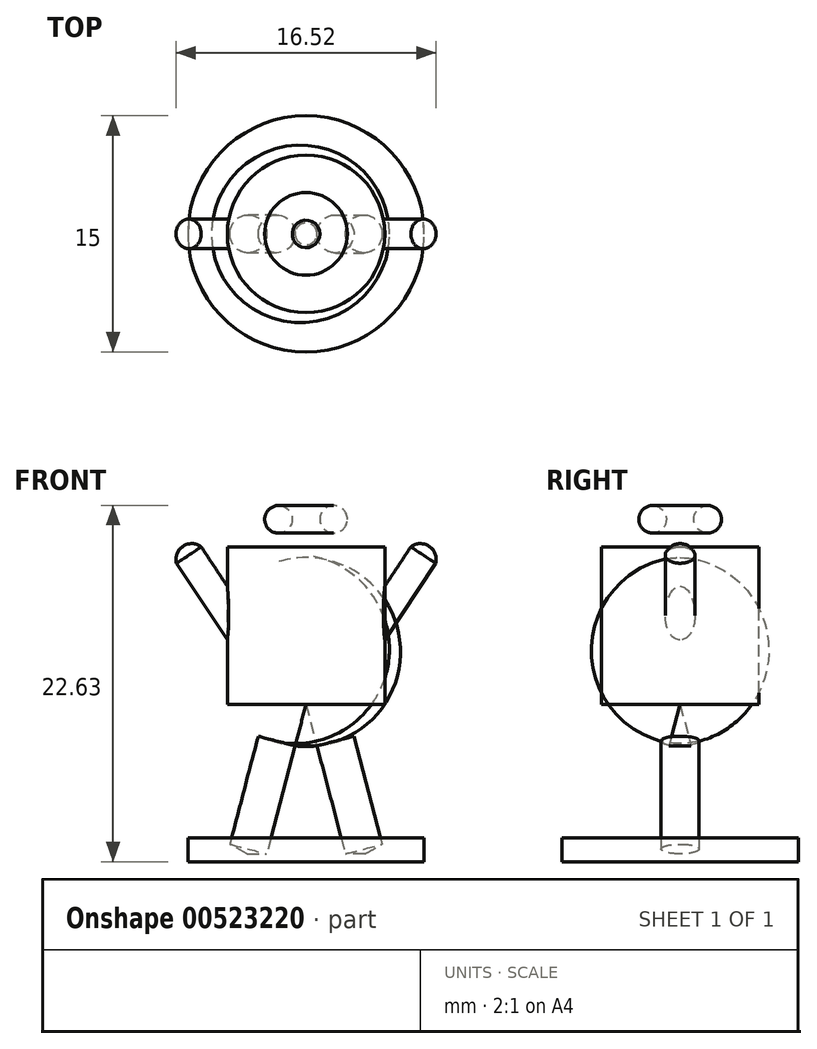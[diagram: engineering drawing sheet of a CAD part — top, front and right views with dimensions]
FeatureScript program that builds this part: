
annotation { "Feature Type Name" : "Feature", "Feature Type Description" : "" }
export const myFeature = defineFeature(function(context is Context, id is Id, definition is map)
    precondition{}
    {
        {
            var Q0;
            Q0=qCreatedBy(makeId("Front.planeOp"),FACE);
            var sketch = newSketch(context, id + "F0", { "sketchPlane" : qUnion([Q0])});
            skLineSegment(sketch, "E0.bottom", {"start": v(-5, 2.5) * mm, "end": v(5, 2.5) * mm});
            skLineSegment(sketch, "E0.top", {"start": v(-5, -7.5) * mm, "end": v(5, -7.5) * mm});
            skLineSegment(sketch, "E0.left", {"start": v(-5, 2.5) * mm, "end": v(-5, -7.5) * mm});
            skLineSegment(sketch, "E0.right", {"start": v(5, 2.5) * mm, "end": v(5, -7.5) * mm});
            skArc(sketch, "E1", {"start": v(5, 2.5) * mm, "mid": v(0, 7.5) * mm, "end": v(-5, 2.5) * mm});
            skCircle(sketch, "E2", {"center": v(-1.75, 4.25) * mm, "radius": 0.88 * mm});
            skCircle(sketch, "E3.MirrorC", {"center": v(1.75, 4.25) * mm, "radius": 0.88 * mm});
            skLineSegment(sketch, "E4.MirrorCS", {"start": v(-5, 0) * mm, "end": v(-5, -3.42) * mm});
            skLineSegment(sketch, "E5.bottom", {"start": v(5, -7.5) * mm, "end": v(2.5, -7.5) * mm});
            skLineSegment(sketch, "E6", {"start": v(0, 7.5) * mm, "end": v(0, 0) * mm});
            skLineSegment(sketch, "E7", {"start": v(0, 2.5) * mm, "end": v(0, -7.5) * mm});
            skLineSegment(sketch, "E8.MirrorCS", {"start": v(-0.02, -5) * mm, "end": v(0, 5) * mm});
            skLineSegment(sketch, "E9", {"start": v(5, 0) * mm, "end": v(6.66, 2.5) * mm});
            skLineSegment(sketch, "E10", {"start": v(6.66, 2.5) * mm, "end": v(8.23, 1.46) * mm});
            skLineSegment(sketch, "E11", {"start": v(8.23, 1.46) * mm, "end": v(5, -3.42) * mm});
            skArc(sketch, "E12", {"start": v(8.23, 1.46) * mm, "mid": v(7.82, 2.54) * mm, "end": v(6.66, 2.5) * mm});
            skLineSegment(sketch, "E13.MirrorCS", {"start": v(-6.68, 2.52) * mm, "end": v(-8.25, 1.48) * mm});
            skArc(sketch, "E14.MirrorCS", {"start": v(-8.25, 1.48) * mm, "mid": v(-7.84, 2.56) * mm, "end": v(-6.68, 2.52) * mm});
            skLineSegment(sketch, "E15.MirrorCS", {"start": v(-5.03, 0.01) * mm, "end": v(-5.03, -3.4) * mm});
            skLineSegment(sketch, "E16.MirrorCS", {"start": v(-8.25, 1.48) * mm, "end": v(-5.03, -3.4) * mm});
            skLineSegment(sketch, "E17.MirrorCS", {"start": v(-5.03, 0.01) * mm, "end": v(-6.68, 2.52) * mm});
            skLineSegment(sketch, "E18", {"start": v(0, -7.5) * mm, "end": v(0, -9.4) * mm});
            skLineSegment(sketch, "E19", {"start": v(2.5, -17) * mm, "end": v(3.75, -17) * mm});
            skLineSegment(sketch, "E20", {"start": v(-3.75, -17) * mm, "end": v(-2.5, -17) * mm});
            skLineSegment(sketch, "E21", {"start": v(7.45, 1.98) * mm, "end": v(5, -1.7) * mm});
            skLineSegment(sketch, "E22", {"start": v(5, -1.7) * mm, "end": v(7.45, 1.98) * mm});
            skLineSegment(sketch, "E23", {"start": v(7.82, 2.54) * mm, "end": v(7.45, 1.98) * mm});
            skLineSegment(sketch, "E24", {"start": v(0, -7.5) * mm, "end": v(2.5, -17) * mm});
            skLineSegment(sketch, "E25", {"start": v(3.75, -17) * mm, "end": v(1.25, -7.5) * mm});
            skLineSegment(sketch, "E26", {"start": v(1.25, -7.5) * mm, "end": v(0, -7.5) * mm});
            skLineSegment(sketch, "E27", {"start": v(0, -7.5) * mm, "end": v(-2.5, -17) * mm});
            skLineSegment(sketch, "E28", {"start": v(-3.75, -17) * mm, "end": v(-1.25, -7.5) * mm});
            skLineSegment(sketch, "E29", {"start": v(-1.25, -7.5) * mm, "end": v(0, -7.5) * mm});
            skArc(sketch, "E30", {"start": v(-5, -7.5) * mm, "mid": v(0, -10.18) * mm, "end": v(5, -7.5) * mm});
            skLineSegment(sketch, "E31", {"start": v(0, -7.5) * mm, "end": v(0, -10.18) * mm});
            skSolve(sketch);
        }
        {
            var Q0;
            Q0=makeQuery(id+"F0.imprint","IMPRINT",FACE,{"disambiguationData":[TD([[makeQuery(id+"F0.imprint","IMPRINT",EDGE,{"derivedFrom":sQuery(id+"F0.wireOp",EDGE,"E3.MirrorC")}),1.0]])]});
            var Q1;
            Q1=sQuery(id+"F0.wireOp",EDGE,"E6");
            revolve(context, id + "F1", {"entities" : qUnion([Q0]), "axis" : qUnion([Q1]), "revolveType" : RevolveType.FULL});
        }
        {
            var Q0;
            {var subQ0=sQuery(id+"F0.wireOp",EDGE,"E0.right");var subQ1=makeQuery(id+"F0.imprint","INTERSECT",VERTEX,{"derivedFrom":[subQ0,sQuery(id+"F0.wireOp",EDGE,"E9")]});Q0=makeQuery(id+"F0.imprint","IMPRINT",FACE,{"disambiguationData":[TD([[makeQuery(id+"F0.imprint","IMPRINT",EDGE,{"disambiguationData":[TD([[subQ1,-1.0]])],"derivedFrom":subQ0}),-1.0]])]});}
            var Q1;
            Q1=sQuery(id+"F0.wireOp",EDGE,"E6");
            revolve(context, id + "F2", {"entities" : qUnion([Q0]), "axis" : qUnion([Q1]), "revolveType" : RevolveType.FULL});
        }
        {
            var Q0;
            Q0=qCreatedBy(makeId("Front.planeOp"),FACE);
            cPlane(context, id + "F3", {"entities" : qUnion([Q0]), "cplaneType" : CPlaneType.OFFSET, "offset" : 5 * mm, "width" : 150 * mm, "height" : 150 * mm});
        }
        {
            var Q0;
            Q0=qCreatedBy(id+"F3.planeOp",FACE);
            var sketch = newSketch(context, id + "F4", { "sketchPlane" : qUnion([Q0])});
            skCircle(sketch, "E32.0", {"center": v(1.75, 4.25) * mm, "radius": 0.88 * mm});
            skCircle(sketch, "E32.1", {"center": v(-1.75, 4.25) * mm, "radius": 0.88 * mm});
            skSolve(sketch);
        }
        {
            var Q0;
            Q0=makeQuery(id+"F4.imprint","IMPRINT",FACE,{"disambiguationData":[TD([[makeQuery(id+"F4.imprint","IMPRINT",EDGE,{"derivedFrom":sQuery(id+"F4.wireOp",EDGE,"E32.1")}),1.0]])]});
            var Q1;
            Q1=makeQuery(id+"F4.imprint","IMPRINT",FACE,{"disambiguationData":[TD([[makeQuery(id+"F4.imprint","IMPRINT",EDGE,{"derivedFrom":sQuery(id+"F4.wireOp",EDGE,"E32.0")}),-1.0]])]});
            extrude(context, id + "F5", {"entities" : qUnion([Q0, Q1]), "operationType" : NewBodyOperationType.REMOVE, "oppositeDirection" : true, "depth" : 1.5 * mm, "offsetDistance" : 25 * mm});
        }
        {
            var Q0;
            {var subQ0=sQuery(id+"F0.wireOp",EDGE,"E11");Q0=makeQuery(id+"F0.imprint","IMPRINT",FACE,{"disambiguationData":[TD([[makeQuery(id+"F0.imprint","IMPRINT",EDGE,{"derivedFrom":subQ0}),-1.0]])]});}
            var Q1;
            {var subQ3=sQuery(id+"F0.wireOp",EDGE,"E23");Q1=makeQuery(id+"F0.imprint","IMPRINT",FACE,{"disambiguationData":[TD([[makeQuery(id+"F0.imprint","IMPRINT",EDGE,{"derivedFrom":subQ3}),1.0]])]});}
            var Q2;
            Q2=sQuery(id+"F0.wireOp",EDGE,"E22");
            revolve(context, id + "F6", {"operationType" : NewBodyOperationType.ADD, "entities" : qUnion([Q0, Q1]), "axis" : qUnion([Q2]), "revolveType" : RevolveType.FULL});
        }
        {
            var Q0;
            Q0=makeQuery(id+"F2.opRevolve","SWEPT_BODY",BODY,{"disambiguationData":[OSD([sQuery(id+"F0.wireOp",EDGE,"E0.bottom"),sQuery(id+"F0.wireOp",EDGE,"E0.top"),sQuery(id+"F0.wireOp",EDGE,"E0.right"),sQuery(id+"F0.wireOp",EDGE,"E5.bottom"),sQuery(id+"F0.wireOp",EDGE,"E7")])]});
            var Q1;
            Q1=qCreatedBy(makeId("Right.planeOp"),FACE);
            mirror(context, id + "F7", {"entities" : qUnion([Q0]), "mirrorPlane" : qUnion([Q1])});
        }
        {
            var Q0;
            Q0=qCreatedBy(makeId("Top.planeOp"),FACE);
            cPlane(context, id + "F8", {"entities" : qUnion([Q0]), "cplaneType" : CPlaneType.OFFSET, "offset" : 16 * mm, "oppositeDirection" : true, "width" : 150 * mm, "height" : 150 * mm});
        }
        {
            var Q0;
            Q0=qCreatedBy(id+"F8.planeOp",FACE);
            var sketch = newSketch(context, id + "F9", { "sketchPlane" : qUnion([Q0])});
            skCircle(sketch, "E33", {"center": v(0, 0) * mm, "radius": 7.5 * mm});
            skSolve(sketch);
        }
        {
            var Q0;
            Q0=makeQuery(id+"F9.imprint","IMPRINT",FACE,{"disambiguationData":[TD([[makeQuery(id+"F9.imprint","IMPRINT",EDGE,{"derivedFrom":sQuery(id+"F9.wireOp",EDGE,"E33")}),1.0]])]});
            extrude(context, id + "F10", {"entities" : qUnion([Q0]), "depth" : -1.5 * mm, "offsetDistance" : 25 * mm});
        }
        {
            var Q0;
            {var subQ5=sQuery(id+"F0.wireOp",EDGE,"E19");Q0=makeQuery(id+"F0.imprint","IMPRINT",FACE,{"disambiguationData":[TD([[makeQuery(id+"F0.imprint","IMPRINT",EDGE,{"derivedFrom":subQ5}),1.0]])]});}
            var Q1;
            {var subQ5=sQuery(id+"F0.wireOp",EDGE,"E26");Q1=makeQuery(id+"F0.imprint","IMPRINT",FACE,{"disambiguationData":[TD([[makeQuery(id+"F0.imprint","IMPRINT",EDGE,{"derivedFrom":subQ5}),1.0]])]});}
            var Q2;
            Q2=sQuery(id+"F0.wireOp",EDGE,"E25");
            revolve(context, id + "F11", {"entities" : qUnion([Q0, Q1]), "axis" : qUnion([Q2]), "revolveType" : RevolveType.FULL});
        }
        {
            var Q0;
            {var subQ5=sQuery(id+"F0.wireOp",EDGE,"E20");Q0=makeQuery(id+"F0.imprint","IMPRINT",FACE,{"disambiguationData":[TD([[makeQuery(id+"F0.imprint","IMPRINT",EDGE,{"derivedFrom":subQ5}),1.0]])]});}
            var Q1;
            {var subQ5=sQuery(id+"F0.wireOp",EDGE,"E29");Q1=makeQuery(id+"F0.imprint","IMPRINT",FACE,{"disambiguationData":[TD([[makeQuery(id+"F0.imprint","IMPRINT",EDGE,{"derivedFrom":subQ5}),-1.0]])]});}
            var Q2;
            Q2=sQuery(id+"F0.wireOp",EDGE,"E28");
            revolve(context, id + "F12", {"entities" : qUnion([Q0, Q1]), "axis" : qUnion([Q2]), "revolveType" : RevolveType.FULL});
        }
        {
            var Q0;
            {var subQ0=sQuery(id+"F0.wireOp",EDGE,"E31");var subQ6=makeQuery(id+"F0.imprint","IMPRINT",VERTEX,{"derivedFrom":subQ0});Q0=makeQuery(id+"F0.imprint","IMPRINT",FACE,{"disambiguationData":[TD([[makeQuery(id+"F0.imprint","IMPRINT",EDGE,{"disambiguationData":[TD([[subQ6,-1.0]])],"derivedFrom":subQ0}),1.0]])]});}
            var Q1;
            {var subQ0=sQuery(id+"F0.wireOp",EDGE,"E26");Q1=makeQuery(id+"F0.imprint","IMPRINT",FACE,{"disambiguationData":[TD([[makeQuery(id+"F0.imprint","IMPRINT",EDGE,{"derivedFrom":subQ0}),1.0]])]});}
            var Q2;
            {var subQ0=sQuery(id+"F0.wireOp",EDGE,"E5.bottom");Q2=makeQuery(id+"F0.imprint","IMPRINT",FACE,{"disambiguationData":[TD([[makeQuery(id+"F0.imprint","IMPRINT",EDGE,{"derivedFrom":subQ0}),1.0]])]});}
            var Q3;
            Q3=sQuery(id+"F0.wireOp",EDGE,"E31");
            revolve(context, id + "F13", {"entities" : qUnion([Q0, Q1, Q2]), "axis" : qUnion([Q3]), "revolveType" : RevolveType.FULL});
        }
    });
